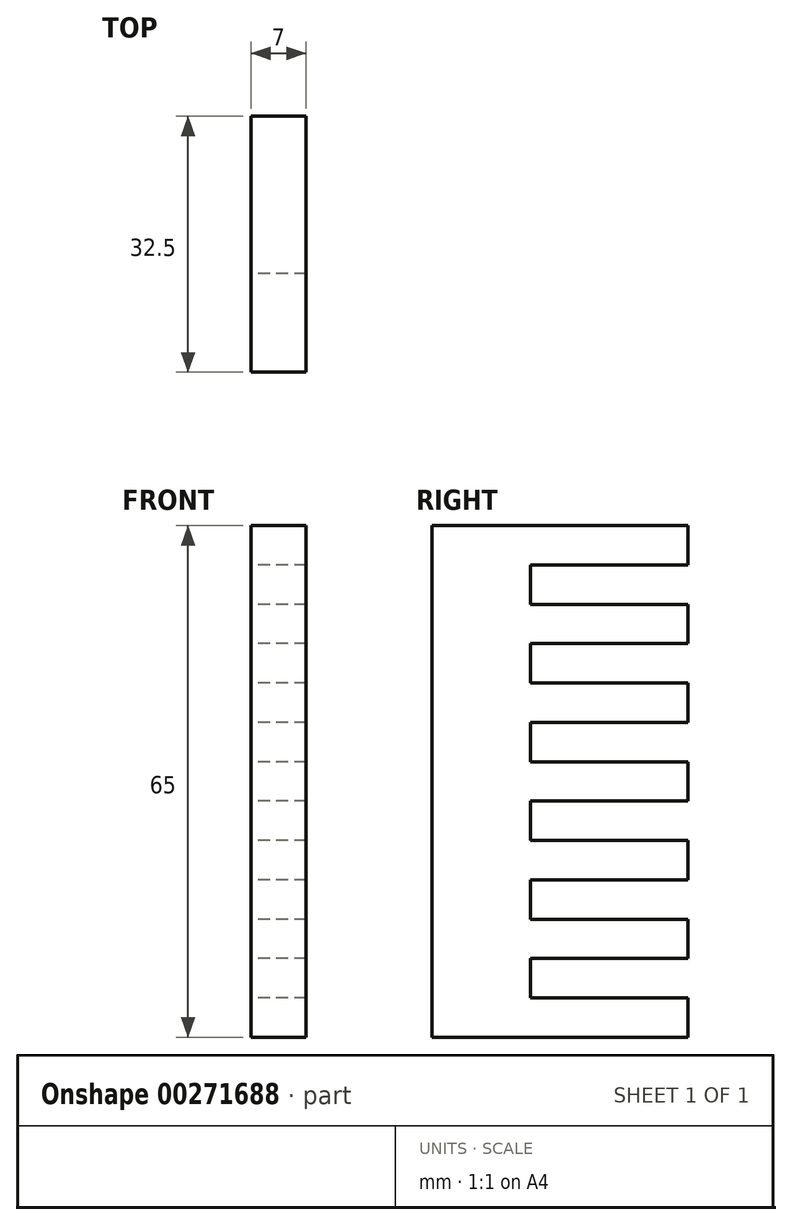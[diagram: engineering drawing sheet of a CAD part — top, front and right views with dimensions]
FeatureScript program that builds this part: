
annotation { "Feature Type Name" : "Feature", "Feature Type Description" : "" }
export const myFeature = defineFeature(function(context is Context, id is Id, definition is map)
    precondition{}
    {
        {
            var Q0;
            Q0=qCreatedBy(makeId("Right.planeOp"),FACE);
            var sketch = newSketch(context, id + "F0", { "sketchPlane" : qUnion([Q0])});
            skLineSegment(sketch, "E0", {"start": v(-21.6, 32.5) * mm, "end": v(10.9, 32.5) * mm});
            skLineSegment(sketch, "E1", {"start": v(10.9, 32.5) * mm, "end": v(10.9, 27.5) * mm});
            skLineSegment(sketch, "E2", {"start": v(10.9, 27.5) * mm, "end": v(-9.1, 27.5) * mm});
            skLineSegment(sketch, "E3", {"start": v(-9.1, 27.5) * mm, "end": v(-9.1, 22.5) * mm});
            skLineSegment(sketch, "E4", {"start": v(-9.1, 22.5) * mm, "end": v(10.9, 22.5) * mm});
            skLineSegment(sketch, "E5", {"start": v(10.9, 22.5) * mm, "end": v(10.9, 17.5) * mm});
            skLineSegment(sketch, "E6", {"start": v(10.9, 17.5) * mm, "end": v(-9.1, 17.5) * mm});
            skLineSegment(sketch, "E7", {"start": v(-9.1, 17.5) * mm, "end": v(-9.1, 12.5) * mm});
            skLineSegment(sketch, "E8", {"start": v(-9.1, 12.5) * mm, "end": v(10.9, 12.5) * mm});
            skLineSegment(sketch, "E9", {"start": v(10.9, 12.5) * mm, "end": v(10.9, 7.5) * mm});
            skLineSegment(sketch, "E10", {"start": v(10.9, 7.5) * mm, "end": v(-9.1, 7.5) * mm});
            skLineSegment(sketch, "E11", {"start": v(-9.1, 7.5) * mm, "end": v(-9.1, 2.5) * mm});
            skLineSegment(sketch, "E12", {"start": v(-9.1, 2.5) * mm, "end": v(10.9, 2.5) * mm});
            skLineSegment(sketch, "E13", {"start": v(10.9, 2.5) * mm, "end": v(10.9, -2.5) * mm});
            skLineSegment(sketch, "E14", {"start": v(10.9, -2.5) * mm, "end": v(-9.1, -2.5) * mm});
            skLineSegment(sketch, "E15", {"start": v(-9.1, -2.5) * mm, "end": v(-9.1, -7.5) * mm});
            skLineSegment(sketch, "E16", {"start": v(-9.1, -7.5) * mm, "end": v(10.9, -7.5) * mm});
            skLineSegment(sketch, "E17", {"start": v(10.9, -7.5) * mm, "end": v(10.9, -12.5) * mm});
            skLineSegment(sketch, "E18", {"start": v(10.9, -12.5) * mm, "end": v(-9.1, -12.5) * mm});
            skLineSegment(sketch, "E19", {"start": v(-9.1, -12.5) * mm, "end": v(-9.1, -17.5) * mm});
            skLineSegment(sketch, "E20", {"start": v(-9.1, -17.5) * mm, "end": v(10.9, -17.5) * mm});
            skLineSegment(sketch, "E21", {"start": v(10.9, -17.5) * mm, "end": v(10.9, -22.5) * mm});
            skLineSegment(sketch, "E22", {"start": v(10.9, -22.5) * mm, "end": v(-9.1, -22.5) * mm});
            skLineSegment(sketch, "E23", {"start": v(-9.1, -22.5) * mm, "end": v(-9.1, -27.5) * mm});
            skLineSegment(sketch, "E24", {"start": v(-9.1, -27.5) * mm, "end": v(10.9, -27.5) * mm});
            skLineSegment(sketch, "E25", {"start": v(10.9, -27.5) * mm, "end": v(10.9, -32.5) * mm});
            skLineSegment(sketch, "E26", {"start": v(10.9, -32.5) * mm, "end": v(-21.6, -32.5) * mm});
            skLineSegment(sketch, "E27", {"start": v(-21.6, -32.5) * mm, "end": v(-21.6, 32.5) * mm});
            skSolve(sketch);
        }
        {
            var Q0;
            Q0=makeQuery(id+"F0.imprint","IMPRINT",FACE,{"disambiguationData":[TD([[makeQuery(id+"F0.imprint","IMPRINT",EDGE,{"derivedFrom":sQuery(id+"F0.wireOp",EDGE,"E0")}),-1.0]])]});
            extrude(context, id + "F1", {"entities" : qUnion([Q0]), "depth" : 7 * mm});
        }
    });
